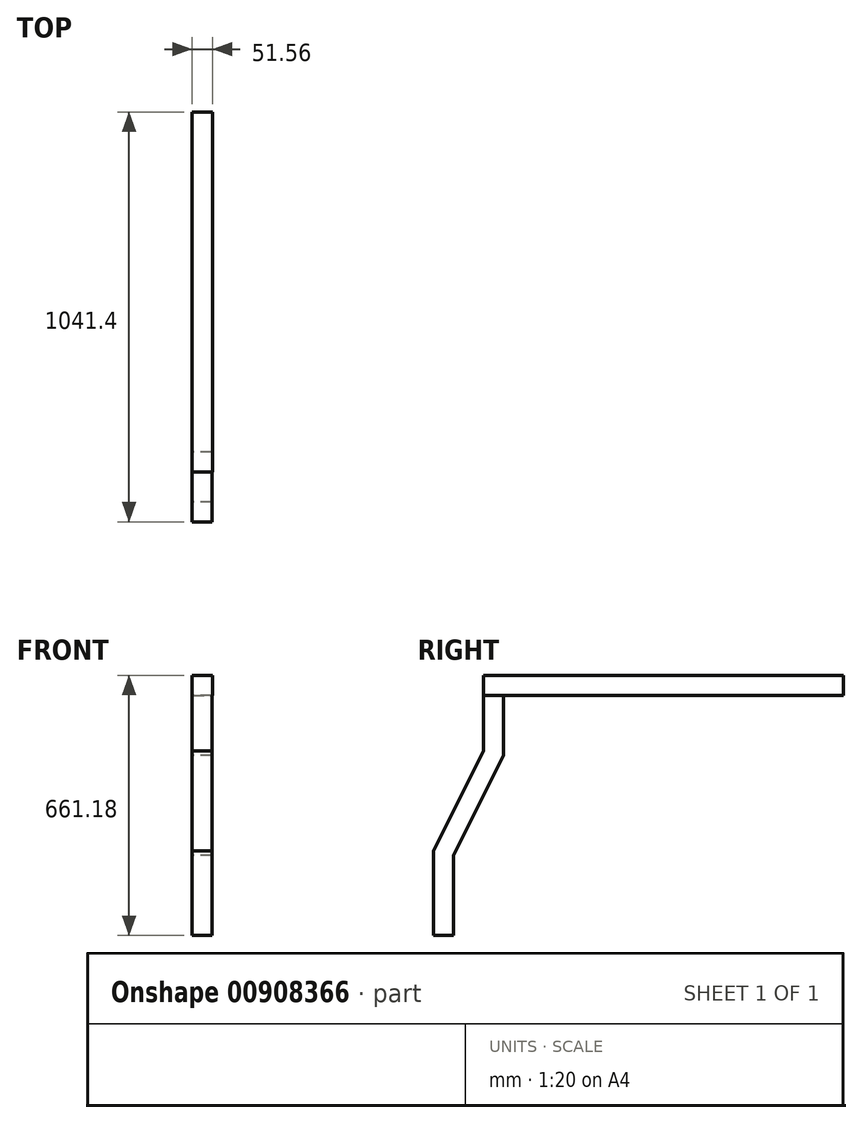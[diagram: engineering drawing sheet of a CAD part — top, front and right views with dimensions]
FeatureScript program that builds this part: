
annotation { "Feature Type Name" : "Feature", "Feature Type Description" : "" }
export const myFeature = defineFeature(function(context is Context, id is Id, definition is map)
    precondition{}
    {
        {
            var Q0;
            Q0=qCreatedBy(makeId("Front.planeOp"),FACE);
            var sketch = newSketch(context, id + "F0", { "sketchPlane" : qUnion([Q0])});
            skLineSegment(sketch, "E0.left", {"start": v(-439.75, 379.34) * mm, "end": v(-439.75, -394.66) * mm});
            skLineSegment(sketch, "E1.bottom", {"start": v(-439.75, -394.66) * mm, "end": v(1610.97, -394.66) * mm});
            skLineSegment(sketch, "E1.left", {"start": v(-439.75, -394.66) * mm, "end": v(-439.75, 939.4) * mm});
            skLineSegment(sketch, "E2.bottom", {"start": v(-439.75, -394.66) * mm, "end": v(-250.97, -394.66) * mm});
            skLineSegment(sketch, "E2.top", {"start": v(-439.75, 939.4) * mm, "end": v(-250.97, 939.4) * mm});
            skLineSegment(sketch, "E2.right", {"start": v(-250.97, -394.66) * mm, "end": v(-250.97, 939.4) * mm});
            skLineSegment(sketch, "E3", {"start": v(1050.78, 939.4) * mm, "end": v(1610.97, 499.99) * mm});
            skLineSegment(sketch, "E4", {"start": v(1610.97, 499.99) * mm, "end": v(1610.97, -394.66) * mm});
            skLineSegment(sketch, "E5", {"start": v(-250.97, 939.4) * mm, "end": v(1050.78, 939.4) * mm});
            skLineSegment(sketch, "E6", {"start": v(1610.97, -394.66) * mm, "end": v(3517.52, -394.66) * mm});
            skLineSegment(sketch, "E7", {"start": v(1610.97, 499.99) * mm, "end": v(3510.77, 313.7) * mm});
            skLineSegment(sketch, "E8", {"start": v(1610.97, -394.66) * mm, "end": v(1888.01, -394.66) * mm});
            skLineSegment(sketch, "E9", {"start": v(1888.01, -394.66) * mm, "end": v(1888.01, 472.82) * mm});
            skLineSegment(sketch, "E10", {"start": v(1888.01, -394.66) * mm, "end": v(3259.71, -394.66) * mm});
            skLineSegment(sketch, "E11", {"start": v(3259.71, -394.66) * mm, "end": v(3259.71, 338.32) * mm});
            skLineSegment(sketch, "E12", {"start": v(-1964.3, -1003.3) * mm, "end": v(-3196.81, -1003.3) * mm});
            skLineSegment(sketch, "E13", {"start": v(-3196.81, -1003.3) * mm, "end": v(4350.14, -1003.3) * mm});
            skCircle(sketch, "E14", {"center": v(2233.34, -573.56) * mm, "radius": 419.1 * mm});
            skLineSegment(sketch, "E15", {"start": v(-439.75, 379.34) * mm, "end": v(-466.68, 379.34) * mm});
            skLineSegment(sketch, "E16", {"start": v(-466.68, 379.34) * mm, "end": v(-466.68, -394.66) * mm});
            skLineSegment(sketch, "E17", {"start": v(-466.68, -394.66) * mm, "end": v(-2636.26, -394.66) * mm});
            skLineSegment(sketch, "E18", {"start": v(-2636.26, -394.66) * mm, "end": v(-2510.94, -394.66) * mm});
            skLineSegment(sketch, "E19", {"start": v(-2510.94, -394.66) * mm, "end": v(-2510.94, 379.34) * mm});
            skLineSegment(sketch, "E20", {"start": v(-2510.94, 379.34) * mm, "end": v(-466.68, 379.34) * mm});
            skLineSegment(sketch, "E21", {"start": v(-2510.94, 379.34) * mm, "end": v(-2510.94, -59.9) * mm});
            skLineSegment(sketch, "E22", {"start": v(-2510.94, -59.9) * mm, "end": v(-2636.26, -59.9) * mm});
            skLineSegment(sketch, "E23", {"start": v(-2636.26, -59.9) * mm, "end": v(-2636.26, -394.66) * mm});
            skLineSegment(sketch, "E24", {"start": v(-2636.26, -394.66) * mm, "end": v(-2636.26, -1003.3) * mm});
            skLineSegment(sketch, "E25", {"start": v(-2636.26, -1003.3) * mm, "end": v(-1292.36, -1003.3) * mm});
            skLineSegment(sketch, "E26", {"start": v(-1292.36, -1003.3) * mm, "end": v(-1292.36, 379.34) * mm});
            skLineSegment(sketch, "E27", {"start": v(-1292.36, -1003.3) * mm, "end": v(-1292.36, -205.89) * mm});
            skLineSegment(sketch, "E28", {"start": v(-1292.36, -205.89) * mm, "end": v(-1292.36, -604.6) * mm});
            skCircle(sketch, "E29", {"center": v(-1292.36, -604.6) * mm, "radius": 419.1 * mm});
            skLineSegment(sketch, "E30", {"start": v(-2510.94, 379.34) * mm, "end": v(-2432.62, 379.34) * mm});
            skLineSegment(sketch, "E31", {"start": v(-2432.62, 379.34) * mm, "end": v(-466.68, 379.34) * mm});
            skLineSegment(sketch, "E32", {"start": v(-2510.94, -59.9) * mm, "end": v(-466.68, -59.9) * mm});
            skLineSegment(sketch, "E33", {"start": v(-466.68, -59.9) * mm, "end": v(-466.68, 379.34) * mm});
            skSolve(sketch);
        }
        {
            var Q0;
            Q0=makeQuery(id+"F0.imprint","IMPRINT",FACE,{"disambiguationData":[TD([[makeQuery(id+"F0.imprint","IMPRINT",EDGE,{"derivedFrom":sQuery(id+"F0.wireOp",EDGE,"E1.bottom")}),1.0]])]});
            var sketch = newSketch(context, id + "F1", { "sketchPlane" : qUnion([Q0])});
            skLineSegment(sketch, "E34", {"start": v(-2438.45, 384.26) * mm, "end": v(-2438.45, 1011.84) * mm});
            skLineSegment(sketch, "E35", {"start": v(-2438.45, 1011.84) * mm, "end": v(-2386.89, 1011.84) * mm});
            skLineSegment(sketch, "E36", {"start": v(-2386.89, 1011.84) * mm, "end": v(-2386.89, 384.26) * mm});
            skLineSegment(sketch, "E37", {"start": v(-2386.89, 384.26) * mm, "end": v(-594.3, 384.26) * mm});
            skLineSegment(sketch, "E38", {"start": v(-594.3, 384.26) * mm, "end": v(-594.3, 1011.84) * mm});
            skLineSegment(sketch, "E39", {"start": v(-594.3, 1011.84) * mm, "end": v(-542.74, 1011.84) * mm});
            skLineSegment(sketch, "E40", {"start": v(-542.74, 1011.84) * mm, "end": v(-542.74, 384.26) * mm});
            skLineSegment(sketch, "E41", {"start": v(-542.74, 384.26) * mm, "end": v(-512.73, 384.26) * mm});
            skLineSegment(sketch, "E42", {"start": v(-2386.89, 1011.84) * mm, "end": v(-594.3, 1011.84) * mm});
            skLineSegment(sketch, "E43", {"start": v(-2438.45, 384.26) * mm, "end": v(-2386.89, 384.26) * mm});
            skLineSegment(sketch, "E44", {"start": v(-594.3, 384.26) * mm, "end": v(-542.74, 384.26) * mm});
            skLineSegment(sketch, "E45", {"start": v(-594.3, 1011.84) * mm, "end": v(-594.3, 1163.94) * mm});
            skLineSegment(sketch, "E46", {"start": v(-594.3, 1163.94) * mm, "end": v(-542.74, 1163.94) * mm});
            skLineSegment(sketch, "E47", {"start": v(-542.74, 1163.94) * mm, "end": v(-542.74, 1011.84) * mm});
            skLineSegment(sketch, "E48", {"start": v(-2438.45, 1011.84) * mm, "end": v(-2438.45, 1163.95) * mm});
            skLineSegment(sketch, "E49", {"start": v(-2386.89, 1011.84) * mm, "end": v(-2386.89, 1163.95) * mm});
            skLineSegment(sketch, "E50", {"start": v(-2386.89, 1163.95) * mm, "end": v(-2438.45, 1163.95) * mm});
            skLineSegment(sketch, "E51", {"start": v(-542.74, 1063.42) * mm, "end": v(1084.55, 1063.42) * mm});
            skLineSegment(sketch, "E52", {"start": v(1084.55, 1063.42) * mm, "end": v(1084.55, 1011.84) * mm});
            skLineSegment(sketch, "E53", {"start": v(1084.55, 1011.84) * mm, "end": v(-542.74, 1011.84) * mm});
            skLineSegment(sketch, "E54", {"start": v(-2438.45, 1063.42) * mm, "end": v(-2386.89, 1063.42) * mm});
            skLineSegment(sketch, "E55", {"start": v(-594.3, 1063.42) * mm, "end": v(-542.74, 1063.42) * mm});
            skLineSegment(sketch, "E56", {"start": v(-2438.45, 1011.84) * mm, "end": v(-2438.45, 884.95) * mm});
            skLineSegment(sketch, "E57", {"start": v(-2438.45, 884.95) * mm, "end": v(-2386.89, 884.95) * mm});
            skLineSegment(sketch, "E58", {"start": v(-594.3, 1011.84) * mm, "end": v(-594.3, 884.94) * mm});
            skLineSegment(sketch, "E59", {"start": v(-594.3, 884.94) * mm, "end": v(-542.74, 884.94) * mm});
            skLineSegment(sketch, "E60", {"start": v(-594.3, 1063.42) * mm, "end": v(-1032.6, 1063.42) * mm});
            skLineSegment(sketch, "E61", {"start": v(-1032.6, 1063.42) * mm, "end": v(-594.3, 1163.94) * mm});
            skLineSegment(sketch, "E62", {"start": v(1084.55, 1063.42) * mm, "end": v(976.92, 1063.42) * mm});
            skLineSegment(sketch, "E63", {"start": v(976.92, 1063.42) * mm, "end": v(-542.74, 1063.42) * mm});
            skLineSegment(sketch, "E64", {"start": v(-542.74, 1163.94) * mm, "end": v(976.92, 1063.42) * mm});
            skLineSegment(sketch, "E65", {"start": v(-2386.89, 1063.42) * mm, "end": v(-626.9, 1063.42) * mm});
            skLineSegment(sketch, "E66", {"start": v(-2438.45, 384.26) * mm, "end": v(-2516.47, 384.26) * mm});
            skLineSegment(sketch, "E67", {"start": v(-2516.47, 384.26) * mm, "end": v(-2555.4, 384.26) * mm});
            skLineSegment(sketch, "E68", {"start": v(1084.55, 1011.84) * mm, "end": v(1084.55, 733.43) * mm});
            skLineSegment(sketch, "E69", {"start": v(773.37, 1011.84) * mm, "end": v(773.37, 924.2) * mm});
            skLineSegment(sketch, "E70", {"start": v(123.19, 1011.84) * mm, "end": v(123.19, 963.13) * mm});
            skSolve(sketch);
        }
        {
            var Q0;
            {var subQ0=sQuery(id+"F1.wireOp",EDGE,"E35");Q0=makeQuery(id+"F1.imprint","IMPRINT",FACE,{"disambiguationData":[TD([[makeQuery(id+"F1.imprint","IMPRINT",EDGE,{"derivedFrom":subQ0}),1.0]])]});}
            extrude(context, id + "F2", {"entities" : qUnion([Q0]), "depth" : 914.4 * mm, "offsetDistance" : 25.4 * mm});
        }
        {
            var Q0;
            Q0=makeQuery(id+"F2.opExtrude","SWEPT_FACE",FACE,{"disambiguationData":[OSD([sQuery(id+"F1.wireOp",EDGE,"E48")])]});
            var sketch = newSketch(context, id + "F3", { "sketchPlane" : qUnion([Q0])});
            skLineSegment(sketch, "E71", {"start": v(863.6, 1011.84) * mm, "end": v(863.6, 859.44) * mm});
            skLineSegment(sketch, "E72", {"start": v(863.6, 859.44) * mm, "end": v(990.6, 605.44) * mm});
            skLineSegment(sketch, "E73", {"start": v(990.6, 605.44) * mm, "end": v(990.6, 402.24) * mm});
            skLineSegment(sketch, "E74", {"start": v(990.6, 402.24) * mm, "end": v(1041.4, 402.24) * mm});
            skLineSegment(sketch, "E75", {"start": v(1041.4, 402.24) * mm, "end": v(1041.4, 617.43) * mm});
            skLineSegment(sketch, "E76", {"start": v(1041.4, 617.43) * mm, "end": v(914.4, 871.43) * mm});
            skLineSegment(sketch, "E77", {"start": v(914.4, 871.43) * mm, "end": v(914.4, 1011.84) * mm});
            skLineSegment(sketch, "E78", {"start": v(914.4, 1011.84) * mm, "end": v(863.6, 1011.84) * mm});
            skLineSegment(sketch, "E79", {"start": v(863.6, 859.44) * mm, "end": v(914.4, 871.43) * mm, "construction": true});
            skLineSegment(sketch, "E80", {"start": v(990.6, 605.44) * mm, "end": v(1041.4, 617.43) * mm, "construction": true});
            skSolve(sketch);
        }
        {
            var Q0;
            Q0 = qSketchRegion(id + "F3", true);
            extrude(context, id + "F4", {"entities" : qUnion([Q0]), "operationType" : NewBodyOperationType.ADD, "oppositeDirection" : true, "depth" : 50.8 * mm, "offsetDistance" : 25.4 * mm});
        }
    });
